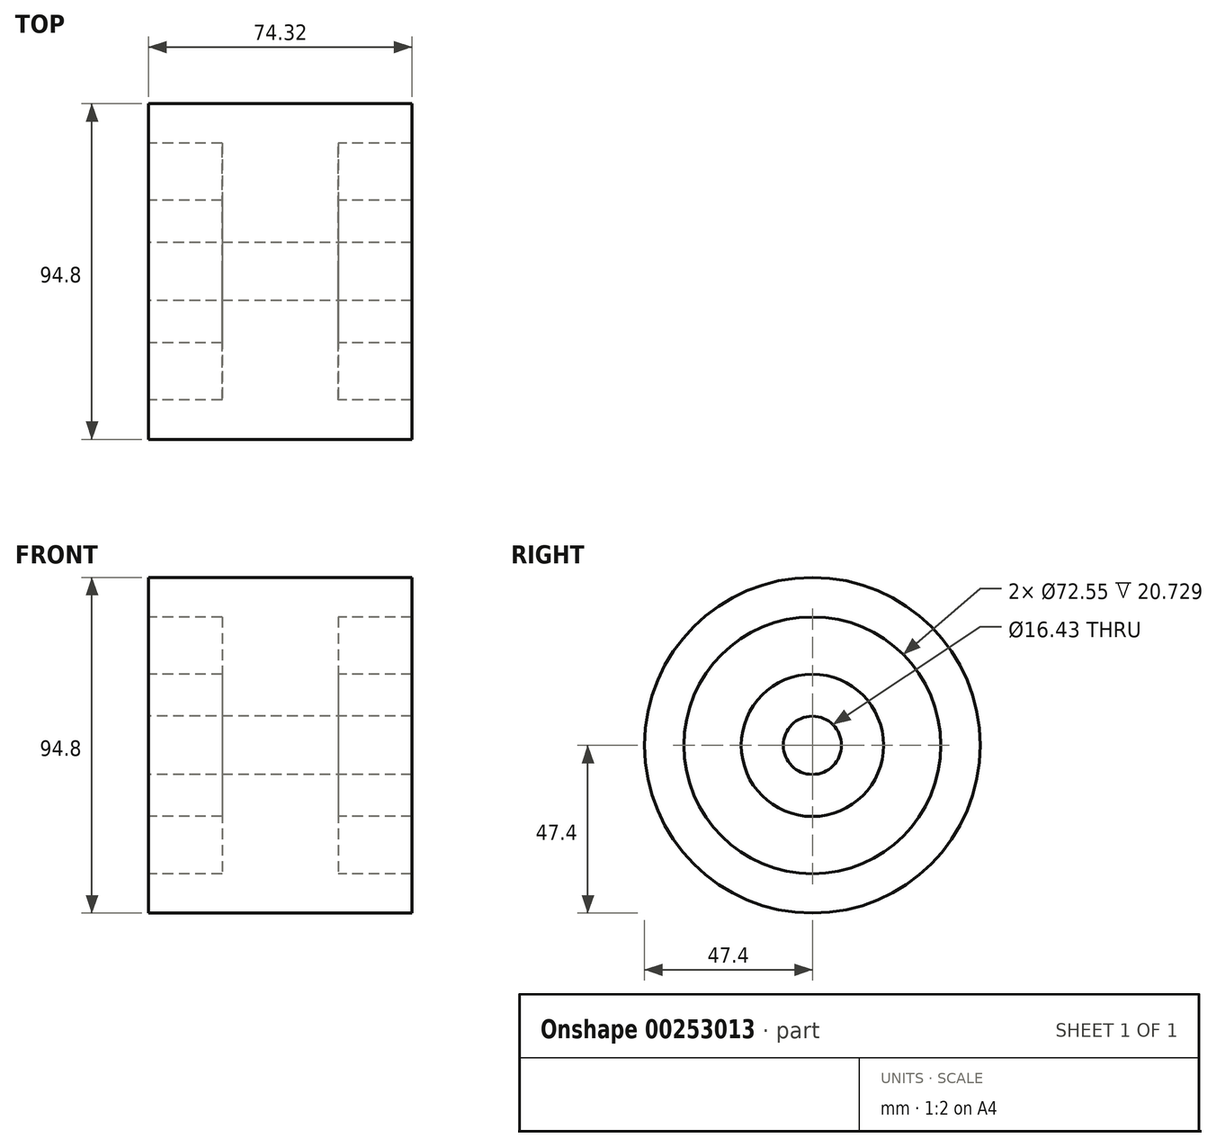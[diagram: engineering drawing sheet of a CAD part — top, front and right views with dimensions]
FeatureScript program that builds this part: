
annotation { "Feature Type Name" : "Feature", "Feature Type Description" : "" }
export const myFeature = defineFeature(function(context is Context, id is Id, definition is map)
    precondition{}
    {
        {
            var Q0;
            Q0=qCreatedBy(makeId("Front.planeOp"),FACE);
            var sketch = newSketch(context, id + "F0", { "sketchPlane" : qUnion([Q0])});
            skLineSegment(sketch, "E0", {"start": v(-72.8, 0) * mm, "end": v(65.22, 0) * mm, "construction": true});
            skLineSegment(sketch, "E1", {"start": v(0, 0) * mm, "end": v(0, 50.18) * mm, "construction": true});
            skLineSegment(sketch, "E2", {"start": v(0, 8.22) * mm, "end": v(37.16, 8.22) * mm});
            skLineSegment(sketch, "E3", {"start": v(37.16, 8.22) * mm, "end": v(37.16, 20.1) * mm});
            skLineSegment(sketch, "E4", {"start": v(37.16, 20.1) * mm, "end": v(16.43, 20.1) * mm});
            skLineSegment(sketch, "E5", {"start": v(16.43, 20.1) * mm, "end": v(16.43, 36.28) * mm});
            skLineSegment(sketch, "E6", {"start": v(16.43, 36.28) * mm, "end": v(37.16, 36.28) * mm});
            skLineSegment(sketch, "E7", {"start": v(37.16, 36.28) * mm, "end": v(37.16, 47.4) * mm});
            skLineSegment(sketch, "E8", {"start": v(37.16, 47.4) * mm, "end": v(0, 47.4) * mm});
            skLineSegment(sketch, "E9.MirrorCS", {"start": v(-37.16, 20.1) * mm, "end": v(-16.43, 20.1) * mm});
            skLineSegment(sketch, "E10.MirrorCS", {"start": v(-37.16, 47.4) * mm, "end": v(0, 47.4) * mm});
            skLineSegment(sketch, "E11.MirrorCS", {"start": v(-16.43, 20.1) * mm, "end": v(-16.43, 36.28) * mm});
            skLineSegment(sketch, "E12.MirrorCS", {"start": v(-37.16, 36.28) * mm, "end": v(-37.16, 47.4) * mm});
            skLineSegment(sketch, "E13.MirrorCS", {"start": v(-37.16, 8.22) * mm, "end": v(-37.16, 20.1) * mm});
            skLineSegment(sketch, "E14.MirrorCS", {"start": v(0, 8.22) * mm, "end": v(-37.16, 8.22) * mm});
            skLineSegment(sketch, "E15.MirrorCS", {"start": v(-16.43, 36.28) * mm, "end": v(-37.16, 36.28) * mm});
            skSolve(sketch);
        }
        {
            var Q0;
            Q0 = qSketchRegion(id + "F0", true);
            var Q1;
            Q1=sQuery(id+"F0.wireOp",EDGE,"E0");
            revolve(context, id + "F1", {"entities" : qUnion([Q0]), "axis" : qUnion([Q1]), "revolveType" : RevolveType.FULL});
        }
    });
